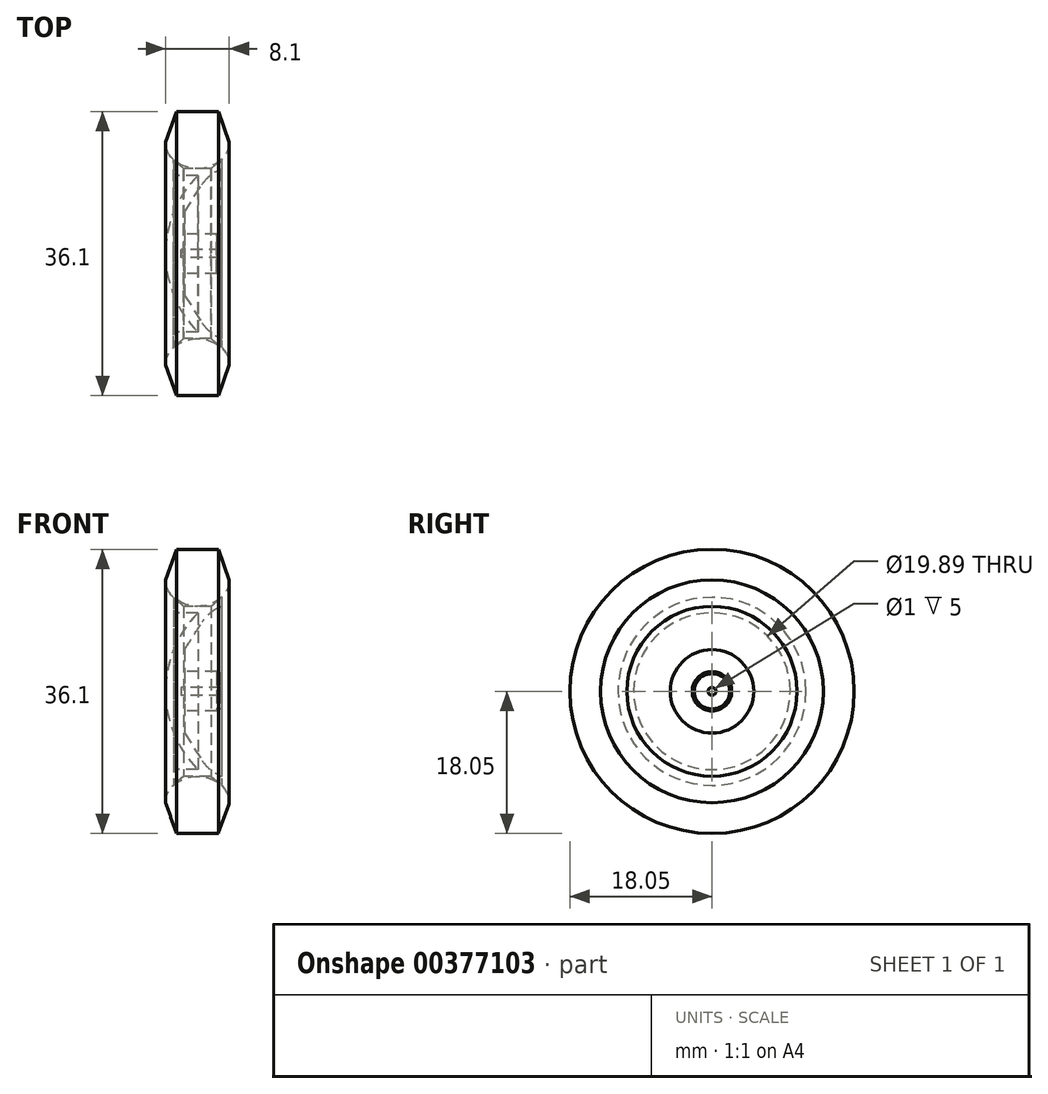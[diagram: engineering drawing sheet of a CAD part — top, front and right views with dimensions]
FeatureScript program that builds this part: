
annotation { "Feature Type Name" : "Feature", "Feature Type Description" : "" }
export const myFeature = defineFeature(function(context is Context, id is Id, definition is map)
    precondition{}
    {
        {
            var Q0;
            Q0=qCreatedBy(makeId("Front.planeOp"),FACE);
            var sketch = newSketch(context, id + "F0", { "sketchPlane" : qUnion([Q0])});
            skLineSegment(sketch, "E0", {"start": v(-4.05, 14.15) * mm, "end": v(4.05, 14.15) * mm, "construction": true});
            skPoint(sketch, "E1", {"position": v(0, 14.15) * mm});
            skEllipticalArc(sketch, "E2", {});
            skPoint(sketch, "E3", {"position": v(0, 10.8) * mm});
            skLineSegment(sketch, "E4", {"start": v(-4.05, 14.15) * mm, "end": v(-2.65, 18.05) * mm});
            skLineSegment(sketch, "E5", {"start": v(-2.65, 18.05) * mm, "end": v(2.65, 18.05) * mm});
            skLineSegment(sketch, "E6", {"start": v(2.65, 18.05) * mm, "end": v(4.05, 14.15) * mm});
            skPoint(sketch, "E7", {"position": v(0, 18.05) * mm});
            skLineSegment(sketch, "E8", {"start": v(4.05, 0) * mm, "end": v(-4.05, 0) * mm, "construction": true});
            skPoint(sketch, "E9", {"position": v(0, 0) * mm});
            const initialGuessF0  = {"E2": [0, 0.01415, 0, 1, 0.00335, 0.00405, 1.5707963267948966, 4.71238898038469]};
            skSetInitialGuess(sketch, initialGuessF0);
            skSolve(sketch);
        }
        {
            var Q0;
            Q0 = qSketchRegion(id + "F0", true);
            var Q1;
            Q1=sQuery(id+"F0.wireOp",EDGE,"E8");
            revolve(context, id + "F1", {"entities" : qUnion([Q0]), "axis" : qUnion([Q1]), "revolveType" : RevolveType.FULL});
        }
        {
            var Q0;
            Q0=qCreatedBy(makeId("Front.planeOp"),FACE);
            var sketch = newSketch(context, id + "F2", { "sketchPlane" : qUnion([Q0])});
            skEllipticalArc(sketch, "E10.0", {"construction": true});
            skPoint(sketch, "E11", {"position": v(-3.05, 11.95) * mm});
            skLineSegment(sketch, "E12", {"start": v(-3.05, 11.95) * mm, "end": v(-3.05, 10.32) * mm});
            skLineSegment(sketch, "E13", {"start": v(1.75, 10.8) * mm, "end": v(-1.75, 10.8) * mm});
            skLineSegment(sketch, "E14", {"start": v(-3.05, 11.95) * mm, "end": v(-1.75, 10.8) * mm});
            skLineSegment(sketch, "E15", {"start": v(-2.68, 9.95) * mm, "end": v(0.05, 9.95) * mm});
            skPoint(sketch, "E16.visualSharp", {"position": v(-3.05, 9.95) * mm});
            skArc(sketch, "E16.filletArc", {"start": v(-3.05, 10.32) * mm, "mid": v(-2.94, 10.05) * mm, "end": v(-2.68, 9.95) * mm});
            skArc(sketch, "E17", {"start": v(0.05, 9.95) * mm, "mid": v(-2.98, 5.38) * mm, "end": v(-4.05, 0) * mm});
            skLineSegment(sketch, "E18", {"start": v(-4.05, 0) * mm, "end": v(-4.05, -5) * mm, "construction": true});
            skPoint(sketch, "E19", {"position": v(3.05, 11.95) * mm});
            skLineSegment(sketch, "E20", {"start": v(3.05, 11.95) * mm, "end": v(1.75, 10.8) * mm});
            skLineSegment(sketch, "E21", {"start": v(3.05, 11.95) * mm, "end": v(3.05, 10.8) * mm});
            skPoint(sketch, "E22", {"position": v(2.45, 10.8) * mm});
            skPoint(sketch, "E23", {"position": v(1.35, 9.95) * mm});
            skLineSegment(sketch, "E24", {"start": v(-4.05, 0) * mm, "end": v(-2.05, 0) * mm});
            skLineSegment(sketch, "E25", {"start": v(2.95, 0.5) * mm, "end": v(2.95, 2.25) * mm});
            skLineSegment(sketch, "E26", {"start": v(2.45, 2.5) * mm, "end": v(-1.65, 2.5) * mm});
            skLineSegment(sketch, "E27", {"start": v(-1.65, 2.5) * mm, "end": v(-1.65, 5.3) * mm});
            skLineSegment(sketch, "E28", {"start": v(2.95, 0.5) * mm, "end": v(-2.05, 0.5) * mm});
            skLineSegment(sketch, "E29", {"start": v(-2.05, 0.5) * mm, "end": v(-2.05, 0) * mm});
            skPoint(sketch, "E30.orphan", {"position": v(2.95, 0) * mm});
            skLineSegment(sketch, "E31", {"start": v(2.95, 2.25) * mm, "end": v(2.45, 2.25) * mm});
            skLineSegment(sketch, "E32", {"start": v(2.45, 2.25) * mm, "end": v(2.45, 2.5) * mm});
            skPoint(sketch, "E33.orphan", {"position": v(2.95, 2.5) * mm});
            skLineSegment(sketch, "E34", {"start": v(3.05, 10.8) * mm, "end": v(2.57, 10.56) * mm});
            skLineSegment(sketch, "E35", {"start": v(-1.65, 5.3) * mm, "end": v(0.6, 8.8) * mm});
            skArc(sketch, "E36.filletArc", {"start": v(2.57, 10.56) * mm, "mid": v(1.47, 9.81) * mm, "end": v(0.6, 8.8) * mm});
            const initialGuessF2  = {"E10.0": [0, 0.01415, -1, 0, 0.00405, 0.00335, 0, 3.141592653589793]};
            skSetInitialGuess(sketch, initialGuessF2);
            skSolve(sketch);
        }
        {
            var Q0;
            Q0 = qSketchRegion(id + "F2", true);
            var Q1;
            Q1=sQuery(id+"F2.wireOp",EDGE,"E24");
            revolve(context, id + "F3", {"entities" : qUnion([Q0]), "axis" : qUnion([Q1]), "revolveType" : RevolveType.FULL});
        }
    });
